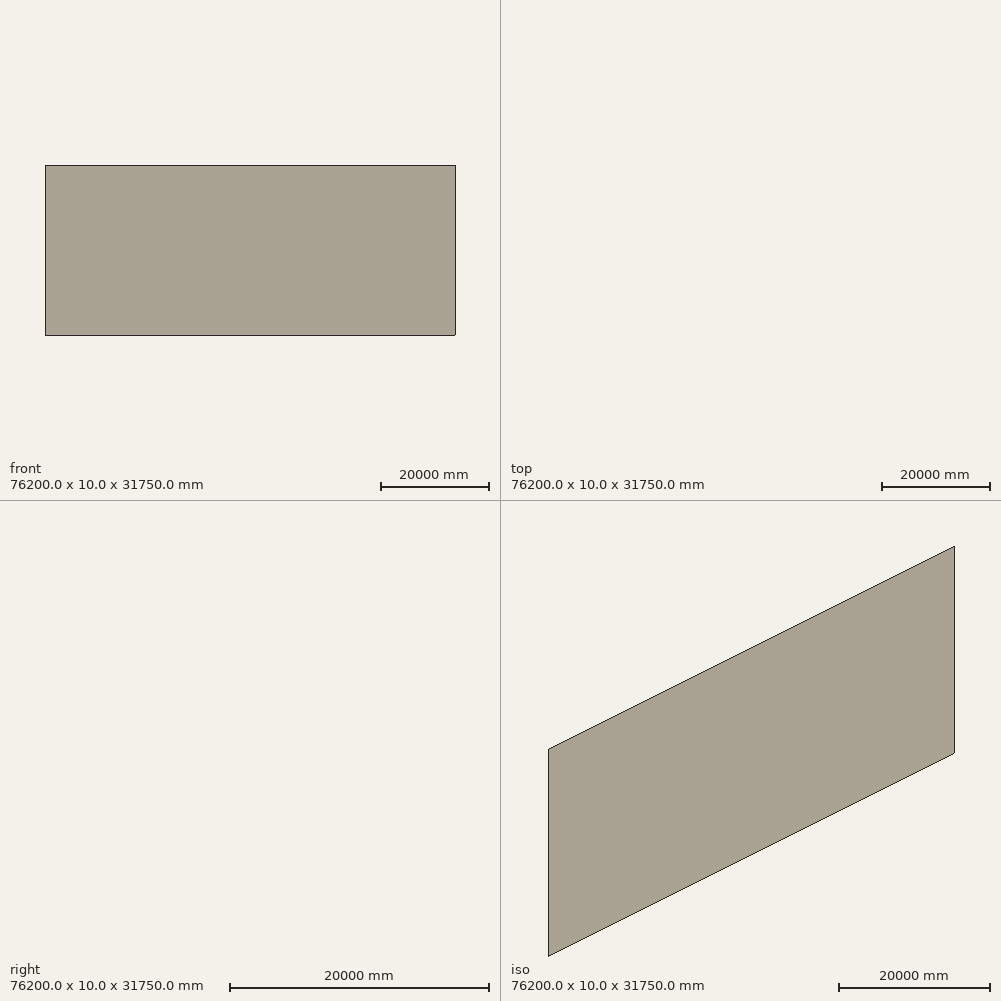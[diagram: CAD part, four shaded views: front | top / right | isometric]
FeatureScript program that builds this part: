
annotation { "Feature Type Name" : "Feature", "Feature Type Description" : "" }
export const myFeature = defineFeature(function(context is Context, id is Id, definition is map)
    precondition{}
    {
        {
            var Q0;
            Q0=qCreatedBy(makeId("Front.planeOp"),FACE);
            var sketch = newSketch(context, id + "F0", { "sketchPlane" : qUnion([Q0])});
            skLineSegment(sketch, "E0.bottom", {"start": v(-27225.31, 0) * mm, "end": v(48974.69, 0) * mm});
            skLineSegment(sketch, "E0.top", {"start": v(-27225.31, 31750) * mm, "end": v(48974.69, 31750) * mm});
            skLineSegment(sketch, "E0.left", {"start": v(-27225.31, 0) * mm, "end": v(-27225.31, 31750) * mm});
            skLineSegment(sketch, "E0.right", {"start": v(48974.69, 0) * mm, "end": v(48974.69, 31750) * mm});
            skSolve(sketch);
        }
        {
            var Q0;
            Q0 = qSketchRegion(id + "F0", true);
            extrude(context, id + "F1", {"entities" : qUnion([Q0]), "depth" : 10 * mm});
        }
    });
